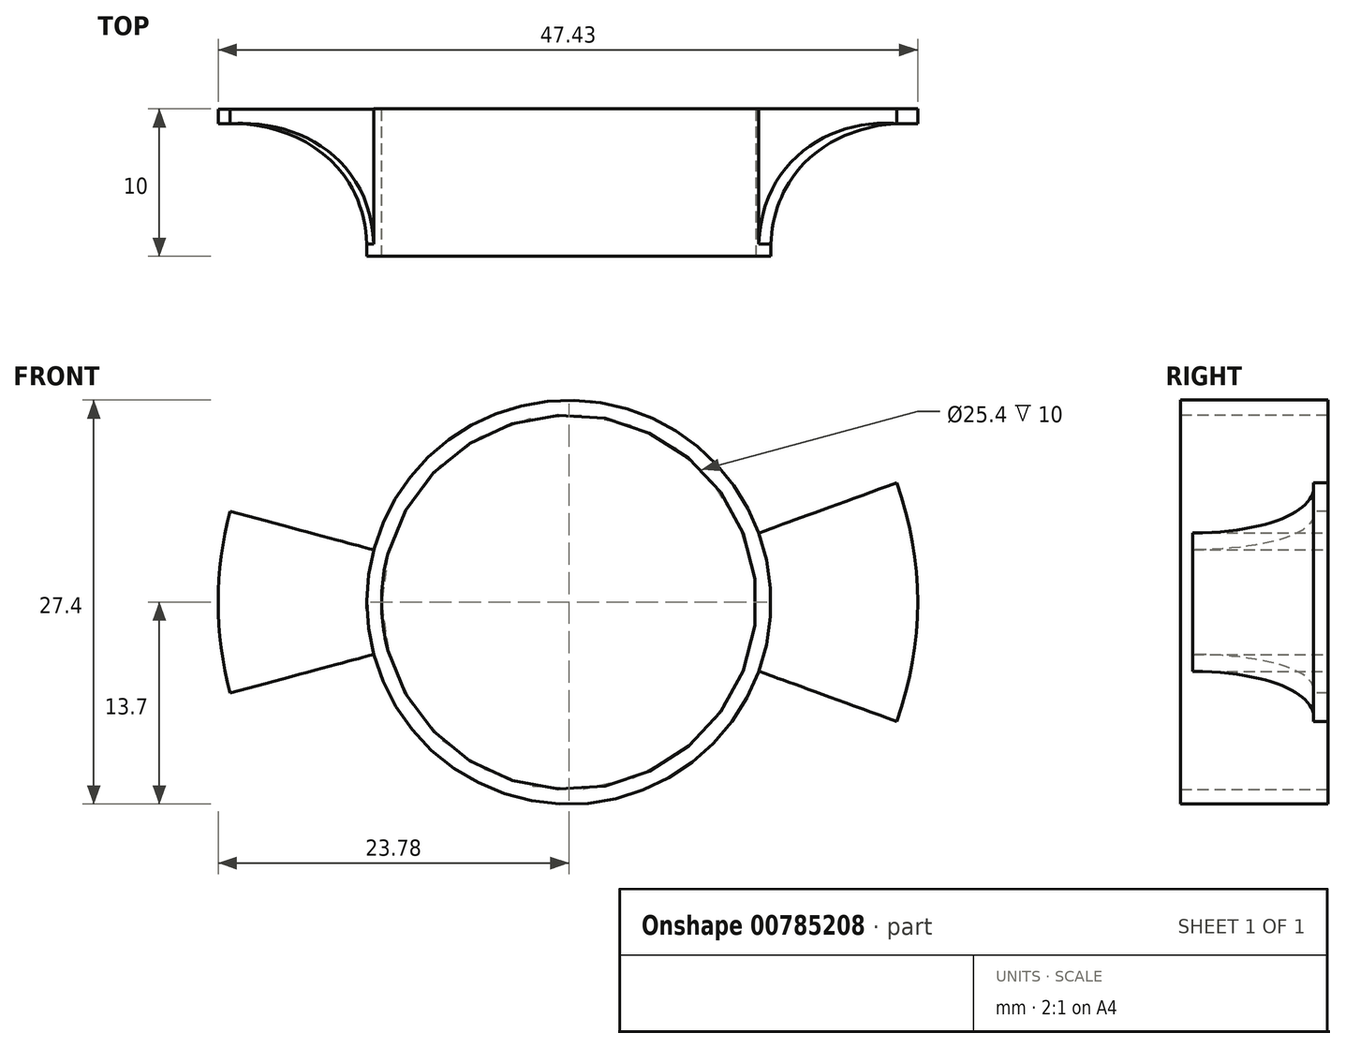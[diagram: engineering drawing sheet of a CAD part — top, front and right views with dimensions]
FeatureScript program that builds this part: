
annotation { "Feature Type Name" : "Feature", "Feature Type Description" : "" }
export const myFeature = defineFeature(function(context is Context, id is Id, definition is map)
    precondition{}
    {
        {
            var Q0;
            Q0=qCreatedBy(makeId("Top.planeOp"),FACE);
            var sketch = newSketch(context, id + "F0", { "sketchPlane" : qUnion([Q0])});
            skLineSegment(sketch, "E0", {"start": v(0, 33) * mm, "end": v(0, -42.93) * mm, "construction": true});
            skCircle(sketch, "E1", {"center": v(0, 0) * mm, "radius": 12.7 * mm, "construction": true});
            skLineSegment(sketch, "E2", {"start": v(12.7, 0) * mm, "end": v(12.7, -10) * mm});
            skLineSegment(sketch, "E3", {"start": v(12.7, -10) * mm, "end": v(13.7, -10) * mm});
            skLineSegment(sketch, "E4", {"start": v(23.65, 0) * mm, "end": v(23.65, -1) * mm});
            skLineSegment(sketch, "E5", {"start": v(12.7, 0) * mm, "end": v(23.65, 0) * mm});
            skFitSpline(sketch, "E6", {"points": [v(23.65, -1) * mm, v(13.7, -10) * mm], "startDerivative": vector(-14.8, 1.14) * mm, "endDerivative": vector(0.72, -19.05) * mm});
            skSolve(sketch);
        }
        {
            var Q0;
            Q0=qCreatedBy(makeId("Top.planeOp"),FACE);
            var sketch = newSketch(context, id + "F1", { "sketchPlane" : qUnion([Q0])});
            skLineSegment(sketch, "E7", {"start": v(0, 33) * mm, "end": v(0, -42.93) * mm, "construction": true});
            skLineSegment(sketch, "E8", {"start": v(-21.5, 3.5) * mm, "end": v(-54.64, 3.5) * mm, "construction": true});
            skCircle(sketch, "E9", {"center": v(0, 0) * mm, "radius": 12.7 * mm, "construction": true});
            skLineSegment(sketch, "E10", {"start": v(12.7, 0) * mm, "end": v(12.7, -10) * mm});
            skLineSegment(sketch, "E11", {"start": v(12.7, -10) * mm, "end": v(13.7, -10) * mm});
            skLineSegment(sketch, "E12", {"start": v(13.7, -10) * mm, "end": v(13.7, 0) * mm});
            skLineSegment(sketch, "E13", {"start": v(12.7, 0) * mm, "end": v(13.7, 0) * mm});
            skSolve(sketch);
        }
        {
            var Q0;
            Q0 = qSketchRegion(id + "F1", true);
            var Q1;
            Q1=sQuery(id+"F1.wireOp",EDGE,"E7");
            revolve(context, id + "F2", {"surfaceOperationType" : NewSurfaceOperationType.NEW, "entities" : qUnion([Q0]), "axis" : qUnion([Q1]), "revolveType" : RevolveType.FULL});
        }
        {
            var Q0;
            Q0 = qSketchRegion(id + "F0", true);
            var Q1;
            Q1=sQuery(id+"F1.wireOp",EDGE,"E7");
            revolve(context, id + "F3", {"operationType" : NewBodyOperationType.ADD, "surfaceOperationType" : NewSurfaceOperationType.NEW, "entities" : qUnion([Q0]), "axis" : qUnion([Q1]), "revolveType" : RevolveType.SYMMETRIC, "angle" : 40 * degree});
        }
        {
            var Q0;
            Q0=qCreatedBy(makeId("Top.planeOp"),FACE);
            var sketch = newSketch(context, id + "F4", { "sketchPlane" : qUnion([Q0])});
            skLineSegment(sketch, "E14", {"start": v(0, 36.94) * mm, "end": v(0, -39.9) * mm, "construction": true});
            skCircle(sketch, "E15", {"center": v(0, 0) * mm, "radius": 12.7 * mm, "construction": true});
            skLineSegment(sketch, "E16.MirrorCS", {"start": v(-12.7, 0) * mm, "end": v(-23.78, 0) * mm});
            skLineSegment(sketch, "E17.MirrorCS", {"start": v(-12.7, 0) * mm, "end": v(-12.7, -10) * mm});
            skLineSegment(sketch, "E18.MirrorCS", {"start": v(-12.7, -10) * mm, "end": v(-13.7, -10) * mm});
            skFitSpline(sketch, "E19.MirrorCS", {"points": [v(-23.78, -1.02) * mm, v(-13.7, -10) * mm], "startDerivative": vector(14.99, 1.15) * mm, "endDerivative": vector(-0.73, -19.27) * mm});
            skLineSegment(sketch, "E20.MirrorCS", {"start": v(-23.78, 0) * mm, "end": v(-23.78, -1.02) * mm});
            skSolve(sketch);
        }
        {
            var Q0;
            Q0=makeQuery(id+"F4.imprint","IMPRINT",FACE,{"disambiguationData":[TD([[makeQuery(id+"F4.imprint","IMPRINT",EDGE,{"derivedFrom":sQuery(id+"F4.wireOp",EDGE,"E16.MirrorCS")}),1.0]])]});
            var Q1;
            Q1=sQuery(id+"F4.wireOp",EDGE,"E14");
            revolve(context, id + "F5", {"operationType" : NewBodyOperationType.ADD, "surfaceOperationType" : NewSurfaceOperationType.NEW, "entities" : qUnion([Q0]), "axis" : qUnion([Q1]), "revolveType" : RevolveType.SYMMETRIC, "angle" : 30 * degree});
        }
    });
